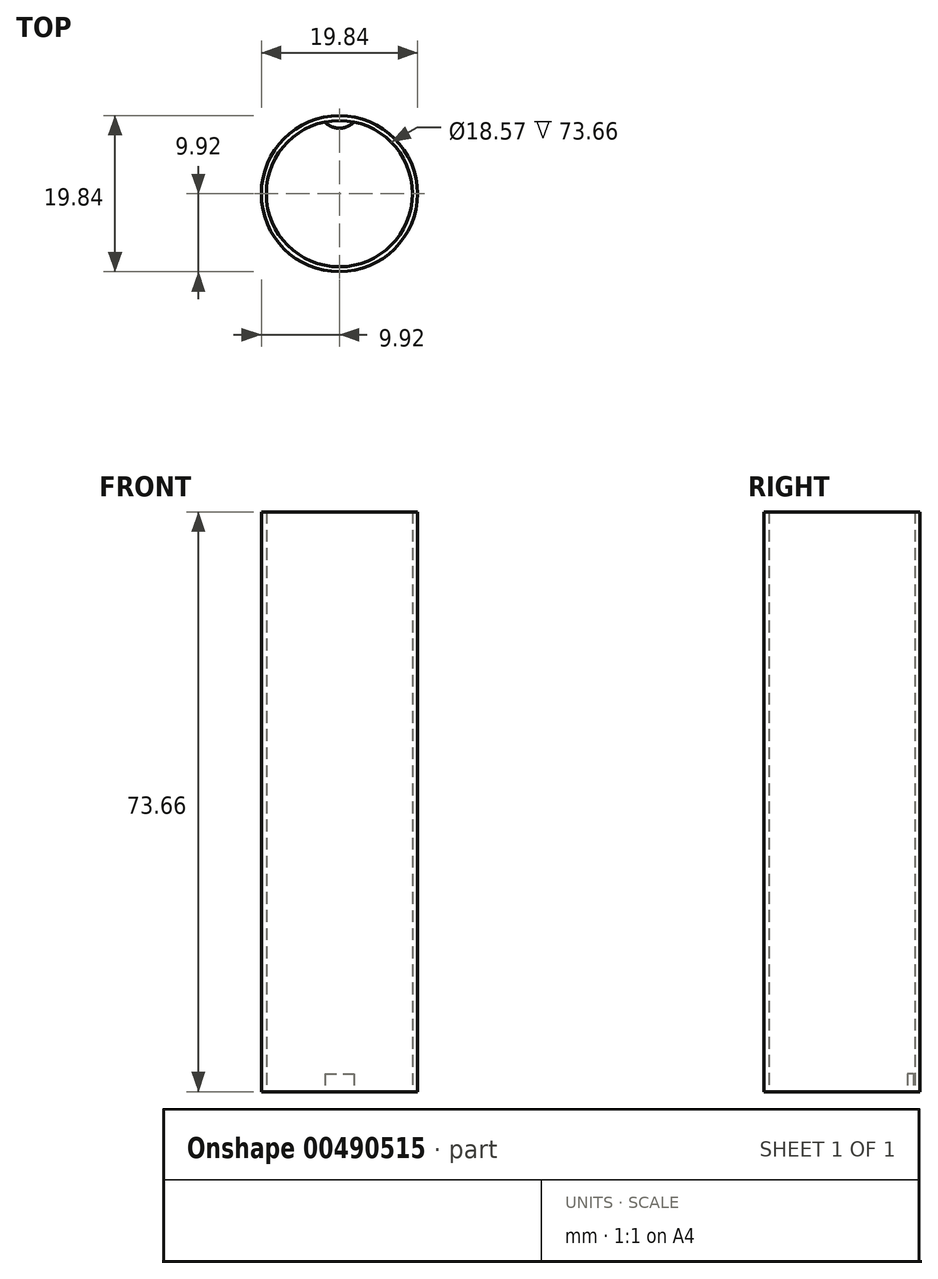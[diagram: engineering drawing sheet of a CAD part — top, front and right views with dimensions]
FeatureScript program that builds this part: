
annotation { "Feature Type Name" : "Feature", "Feature Type Description" : "" }
export const myFeature = defineFeature(function(context is Context, id is Id, definition is map)
    precondition{}
    {
        {
            var Q0;
            Q0=qCreatedBy(makeId("Top.planeOp"),FACE);
            var sketch = newSketch(context, id + "F0", { "sketchPlane" : qUnion([Q0])});
            skCircle(sketch, "E0", {"center": v(0, 0) * mm, "radius": 9.28 * mm});
            skCircle(sketch, "E1", {"center": v(0, 0) * mm, "radius": 9.92 * mm});
            skSolve(sketch);
        }
        {
            var Q0;
            Q0 = qSketchRegion(id + "F0", true);
            extrude(context, id + "F1", {"entities" : qUnion([Q0]), "depth" : 73.66 * mm});
        }
        {
            var Q0;
            Q0=qCreatedBy(makeId("Top.planeOp"),FACE);
            var sketch = newSketch(context, id + "F2", { "sketchPlane" : qUnion([Q0])});
            skArc(sketch, "E2.0", {"start": v(1.83, 9.1) * mm, "mid": v(0, 9.28) * mm, "end": v(-1.83, 9.1) * mm});
            skLineSegment(sketch, "E3", {"start": v(0, 0) * mm, "end": v(0, 9.28) * mm, "construction": true});
            skArc(sketch, "E4", {"start": v(-1.83, 9.1) * mm, "mid": v(0, 8.32) * mm, "end": v(1.83, 9.1) * mm});
            skCircle(sketch, "E5", {"center": v(0, 0) * mm, "radius": 8.83 * mm, "construction": true});
            skSolve(sketch);
        }
        {
            var Q0;
            Q0 = qSketchRegion(id + "F2", true);
            extrude(context, id + "F3", {"entities" : qUnion([Q0]), "depth" : 2.3 * mm});
        }
    });
